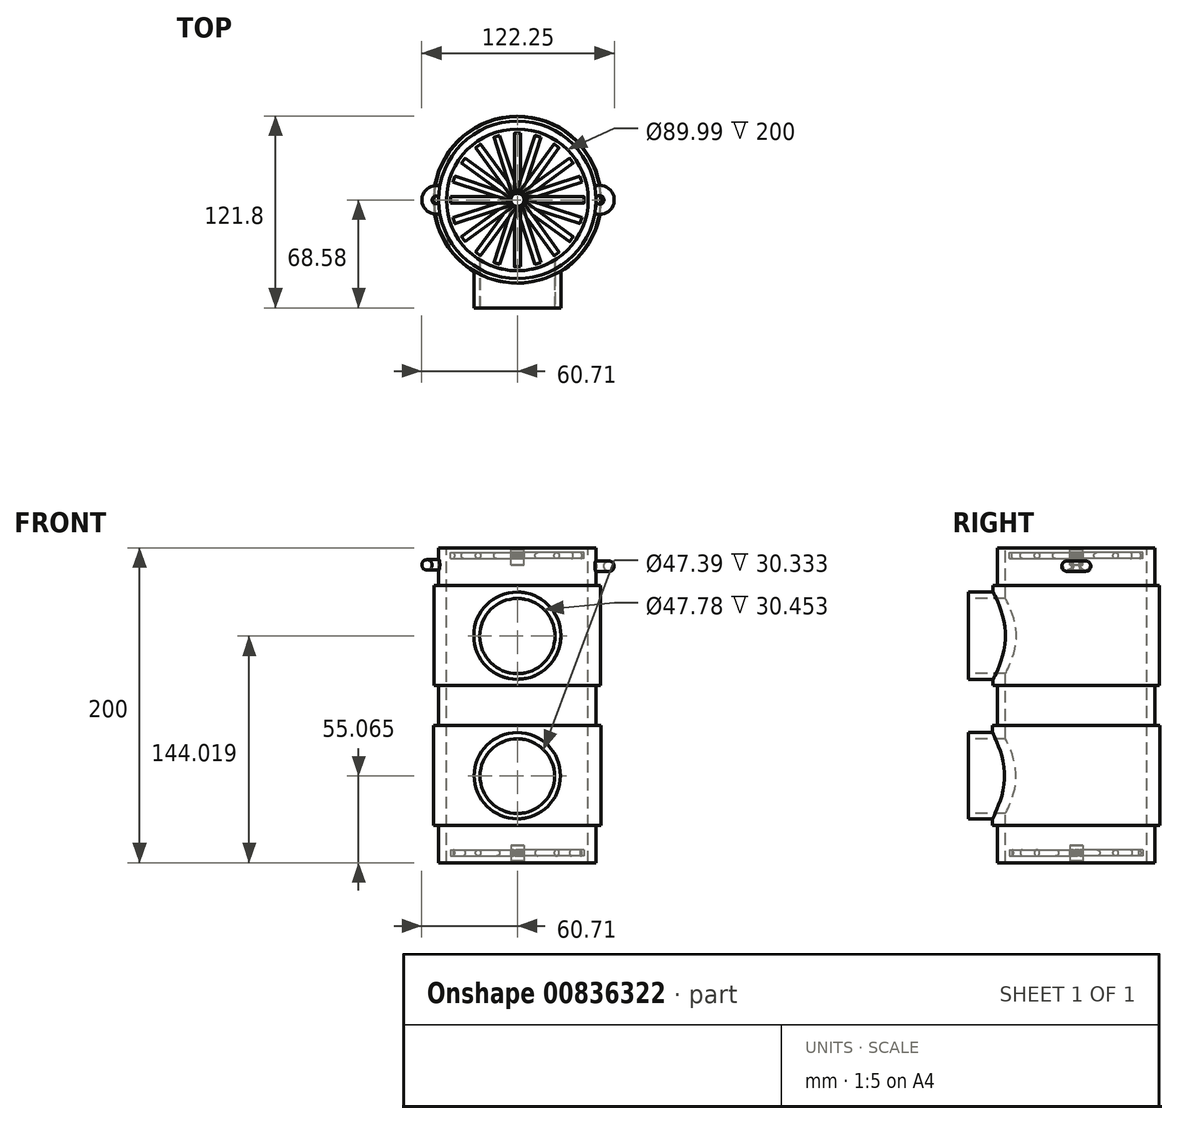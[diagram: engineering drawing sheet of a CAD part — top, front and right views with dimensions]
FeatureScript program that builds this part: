
annotation { "Feature Type Name" : "Feature", "Feature Type Description" : "" }
export const myFeature = defineFeature(function(context is Context, id is Id, definition is map)
    precondition{}
    {
        {
            var Q0;
            Q0=qCreatedBy(makeId("Top.planeOp"),FACE);
            var sketch = newSketch(context, id + "F0", { "sketchPlane" : qUnion([Q0])});
            skCircle(sketch, "E0", {"center": v(0, 0) * mm, "radius": 50 * mm});
            skSolve(sketch);
        }
        {
            var Q0;
            Q0=makeQuery(id+"F0.imprint","IMPRINT",FACE,{"disambiguationData":[TD([[makeQuery(id+"F0.imprint","IMPRINT",EDGE,{"derivedFrom":sQuery(id+"F0.wireOp",EDGE,"E0")}),1.0]])]});
            extrude(context, id + "F1", {"entities" : qUnion([Q0]), "endBound" : BoundingType.SYMMETRIC, "depth" : 200 * mm, "offsetDistance" : 25.4 * mm});
        }
        {
            var Q0;
            Q0=qCreatedBy(makeId("Top.planeOp"),FACE);
            cPlane(context, id + "F2", {"entities" : qUnion([Q0]), "cplaneType" : CPlaneType.OFFSET, "offset" : 12.7 * mm, "width" : 152.4 * mm, "height" : 152.4 * mm});
        }
        {
            var Q0;
            Q0=qCreatedBy(id+"F2.planeOp",FACE);
            var sketch = newSketch(context, id + "F3", { "sketchPlane" : qUnion([Q0])});
            skCircle(sketch, "E1", {"center": v(0, 0) * mm, "radius": 52.86 * mm});
            skSolve(sketch);
        }
        {
            var Q0;
            Q0 = qSketchRegion(id + "F3", true);
            extrude(context, id + "F4", {"entities" : qUnion([Q0]), "operationType" : NewBodyOperationType.ADD, "depth" : 63.5 * mm, "offsetDistance" : 25.4 * mm});
        }
        {
            var Q0;
            Q0=qCreatedBy(makeId("Top.planeOp"),FACE);
            cPlane(context, id + "F5", {"entities" : qUnion([Q0]), "cplaneType" : CPlaneType.OFFSET, "offset" : 12.7 * mm, "oppositeDirection" : true, "width" : 152.4 * mm, "height" : 152.4 * mm});
        }
        {
            var Q0;
            Q0=qCreatedBy(id+"F5.planeOp",FACE);
            var sketch = newSketch(context, id + "F6", { "sketchPlane" : qUnion([Q0])});
            skCircle(sketch, "E2", {"center": v(0, 0) * mm, "radius": 53.22 * mm});
            skSolve(sketch);
        }
        {
            var Q0;
            Q0 = qSketchRegion(id + "F6", true);
            extrude(context, id + "F7", {"entities" : qUnion([Q0]), "operationType" : NewBodyOperationType.ADD, "oppositeDirection" : true, "depth" : 63.5 * mm, "offsetDistance" : 25.4 * mm});
        }
        {
            var Q0;
            Q0=qCreatedBy(makeId("Front.planeOp"),FACE);
            cPlane(context, id + "F8", {"entities" : qUnion([Q0]), "cplaneType" : CPlaneType.OFFSET, "offset" : 68.58 * mm, "width" : 152.4 * mm, "height" : 152.4 * mm});
        }
        {
            var Q0;
            Q0=qCreatedBy(id+"F8.planeOp",FACE);
            var sketch = newSketch(context, id + "F9", { "sketchPlane" : qUnion([Q0])});
            skCircle(sketch, "E3", {"center": v(0, 44.3) * mm, "radius": 27.68 * mm});
            skCircle(sketch, "E4", {"center": v(0, -44.66) * mm, "radius": 27.4 * mm});
            skSolve(sketch);
        }
        {
            var Q0;
            Q0 = qSketchRegion(id + "F9", true);
            extrude(context, id + "F10", {"entities" : qUnion([Q0]), "operationType" : NewBodyOperationType.ADD, "endBound" : BoundingType.UP_TO_NEXT, "oppositeDirection" : true, "depth" : 25.4 * mm, "offsetDistance" : 25.4 * mm});
        }
        {
            var Q0;
            Q0=qCreatedBy(makeId("Top.planeOp"),FACE);
            var sketch = newSketch(context, id + "F11", { "sketchPlane" : qUnion([Q0])});
            skCircle(sketch, "E5", {"center": v(0, 0) * mm, "radius": 45 * mm});
            skSolve(sketch);
        }
        {
            var Q0;
            Q0 = qSketchRegion(id + "F11", true);
            extrude(context, id + "F12", {"entities" : qUnion([Q0]), "operationType" : NewBodyOperationType.REMOVE, "endBound" : BoundingType.SYMMETRIC, "oppositeDirection" : true, "depth" : 208.28 * mm, "offsetDistance" : 25.4 * mm});
        }
        {
            var Q0;
            Q0=qCreatedBy(id+"F8.planeOp",FACE);
            var sketch = newSketch(context, id + "F13", { "sketchPlane" : qUnion([Q0])});
            skCircle(sketch, "E6", {"center": v(0, 44.02) * mm, "radius": 23.9 * mm});
            skCircle(sketch, "E7", {"center": v(0, -44.94) * mm, "radius": 23.7 * mm});
            skSolve(sketch);
        }
        {
            var Q0;
            Q0 = qSketchRegion(id + "F13", true);
            extrude(context, id + "F14", {"entities" : qUnion([Q0]), "operationType" : NewBodyOperationType.REMOVE, "endBound" : BoundingType.UP_TO_NEXT, "oppositeDirection" : true, "depth" : 25.4 * mm, "offsetDistance" : 25.4 * mm});
        }
        {
            var Q0;
            Q0=qCreatedBy(makeId("Top.planeOp"),FACE);
            cPlane(context, id + "F15", {"entities" : qUnion([Q0]), "cplaneType" : CPlaneType.OFFSET, "offset" : 99.06 * mm, "width" : 152.4 * mm, "height" : 152.4 * mm});
        }
        {
            var Q0;
            Q0=qCreatedBy(id+"F15.planeOp",FACE);
            var sketch = newSketch(context, id + "F16", { "sketchPlane" : qUnion([Q0])});
            skCircle(sketch, "E8", {"center": v(0, 0) * mm, "radius": 4.17 * mm});
            skSolve(sketch);
        }
        {
            var Q0;
            Q0 = qSketchRegion(id + "F16", true);
            extrude(context, id + "F17", {"entities" : qUnion([Q0]), "oppositeDirection" : true, "depth" : 10 * mm, "offsetDistance" : 25.4 * mm});
        }
        {
            var Q0;
            Q0=qCreatedBy(makeId("Front.planeOp"),FACE);
            var sketch = newSketch(context, id + "F18", { "sketchPlane" : qUnion([Q0])});
            skCircle(sketch, "E9", {"center": v(0, 95.14) * mm, "radius": 1.97 * mm});
            skSolve(sketch);
        }
        {
            var Q0;
            Q0 = qSketchRegion(id + "F18", true);
            extrude(context, id + "F19", {"entities" : qUnion([Q0]), "operationType" : NewBodyOperationType.ADD, "depth" : 42.42 * mm, "offsetDistance" : 25.4 * mm});
        }
        {
            var Q0;
            Q0=makeQuery(id+"F17.opExtrude","SWEPT_BODY",BODY,{"disambiguationData":[OSD([sQuery(id+"F16.wireOp",EDGE,"E8")])]});
            var Q1;
            Q1=makeQuery(id+"F17.opExtrude","SWEPT_FACE",FACE,{"disambiguationData":[OSD([sQuery(id+"F16.wireOp",EDGE,"E8")])]});
            circularPattern(context, id + "F20", {"entities" : qUnion([Q0]), "axis" : qUnion([Q1]), "angle" : 360 * degree, "instanceCount" : 20, "equalSpace" : true});
        }
        {
            var Q0;
            Q0=qCreatedBy(makeId("Top.planeOp"),FACE);
            cPlane(context, id + "F21", {"entities" : qUnion([Q0]), "cplaneType" : CPlaneType.OFFSET, "offset" : 98.8 * mm, "oppositeDirection" : true, "width" : 152.4 * mm, "height" : 152.4 * mm});
        }
        {
            var Q0;
            Q0=qCreatedBy(id+"F21.planeOp",FACE);
            var sketch = newSketch(context, id + "F22", { "sketchPlane" : qUnion([Q0])});
            skCircle(sketch, "E10", {"center": v(0, 0) * mm, "radius": 4.17 * mm});
            skSolve(sketch);
        }
        {
            var Q0;
            Q0 = qSketchRegion(id + "F22", true);
            extrude(context, id + "F23", {"entities" : qUnion([Q0]), "depth" : 10 * mm, "offsetDistance" : 25.4 * mm});
        }
        {
            var Q0;
            Q0=qCreatedBy(makeId("Front.planeOp"),FACE);
            var sketch = newSketch(context, id + "F24", { "sketchPlane" : qUnion([Q0])});
            skCircle(sketch, "E11", {"center": v(0, -93.65) * mm, "radius": 1.97 * mm});
            skSolve(sketch);
        }
        {
            var Q0;
            Q0 = qSketchRegion(id + "F24", true);
            extrude(context, id + "F25", {"entities" : qUnion([Q0]), "operationType" : NewBodyOperationType.ADD, "depth" : 42.42 * mm, "offsetDistance" : 25.4 * mm});
        }
        {
            var Q0;
            Q0=makeQuery(id+"F23.opExtrude","SWEPT_BODY",BODY,{"disambiguationData":[OSD([sQuery(id+"F22.wireOp",EDGE,"E10")])]});
            var Q1;
            Q1=makeQuery(id+"F23.opExtrude","SWEPT_FACE",FACE,{"disambiguationData":[OSD([sQuery(id+"F22.wireOp",EDGE,"E10")])]});
            circularPattern(context, id + "F26", {"entities" : qUnion([Q0]), "axis" : qUnion([Q1]), "angle" : 360 * degree, "instanceCount" : 20, "equalSpace" : true});
        }
        {
            var Q0;
            Q0=qCreatedBy(makeId("Front.planeOp"),FACE);
            var sketch = newSketch(context, id + "F27", { "sketchPlane" : qUnion([Q0])});
            skCircle(sketch, "E12", {"center": v(58.27, 88.45) * mm, "radius": 3.27 * mm});
            skSolve(sketch);
        }
        {
            var Q0;
            Q0=qCreatedBy(id+"F15.planeOp",FACE);
            cPlane(context, id + "F28", {"entities" : qUnion([Q0]), "cplaneType" : CPlaneType.OFFSET, "offset" : 10.16 * mm, "oppositeDirection" : true, "width" : 152.4 * mm, "height" : 152.4 * mm});
        }
        {
            var Q0;
            Q0=qCreatedBy(id+"F28.planeOp",FACE);
            var sketch = newSketch(context, id + "F29", { "sketchPlane" : qUnion([Q0])});
            skArc(sketch, "E13", {"start": v(47.93, -4.04) * mm, "mid": v(58.17, 0.1) * mm, "end": v(47.8, 3.89) * mm});
            skSolve(sketch);
        }
        {
            var Q0;
            Q0=makeQuery(id+"F27.imprint","IMPRINT",FACE,{"disambiguationData":[TD([[makeQuery(id+"F27.imprint","IMPRINT",EDGE,{"derivedFrom":sQuery(id+"F27.wireOp",EDGE,"E12")}),1.0]])]});
            var Q1;
            Q1=sQuery(id+"F29.wireOp",EDGE,"E13");
            sweep(context, id + "F30", {"operationType" : NewBodyOperationType.ADD, "profiles" : qUnion([Q0]), "path" : qUnion([Q1])});
        }
        {
            var Q0;
            Q0=qCreatedBy(makeId("Front.planeOp"),FACE);
            var sketch = newSketch(context, id + "F31", { "sketchPlane" : qUnion([Q0])});
            skCircle(sketch, "E14", {"center": v(-57.44, 89.27) * mm, "radius": 3.27 * mm});
            skSolve(sketch);
        }
        {
            var Q0;
            Q0=qCreatedBy(id+"F28.planeOp",FACE);
            var sketch = newSketch(context, id + "F32", { "sketchPlane" : qUnion([Q0])});
            skArc(sketch, "E15", {"start": v(-48.18, 4.59) * mm, "mid": v(-57.48, -0.04) * mm, "end": v(-48.13, -4.55) * mm});
            skSolve(sketch);
        }
        {
            var Q0;
            Q0=makeQuery(id+"F31.imprint","IMPRINT",FACE,{"disambiguationData":[TD([[makeQuery(id+"F31.imprint","IMPRINT",EDGE,{"derivedFrom":sQuery(id+"F31.wireOp",EDGE,"E14")}),1.0]])]});
            var Q1;
            Q1=sQuery(id+"F32.wireOp",EDGE,"E15");
            sweep(context, id + "F33", {"operationType" : NewBodyOperationType.ADD, "profiles" : qUnion([Q0]), "path" : qUnion([Q1])});
        }
    });
